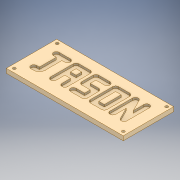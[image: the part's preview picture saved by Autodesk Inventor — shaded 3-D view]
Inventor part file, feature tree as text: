
AUTODESK INVENTOR PART (.ipt)
format: ipt  version: 2017 (Build 210142000, 142)  size: 520,192 bytes
history: native  units: mm
features: sketch x2, extrude x2
ambient origin geometry x8: Origin, YZ Plane, XZ Plane, XY Plane, X Axis, Y Axis, Z Axis, Center Point
bodies: Solid1 (feature_tree)
feature tree (4):
  sketch  "Sketch1"  dims[d2=26.0mm d3=6.5mm]
  extrude  "Extrusion1"  Depth=6.5mm
  extrude  "Extrusion2"  Depth=13.0mm
  sketch  "Sketch2"  dims[d4=13.0mm d11=13.0mm d12=6.5mm d13=13.0mm d16=39.0mm d17=39.0mm d18=6.5mm d19=52.0mm d20=6.5mm d22=13.0mm d23=19.5mm d24=13.0mm d29=13.0mm d30=13.0mm d31=13.0mm d32=13.0mm d35=26.0mm d36=52.0mm d37=13.0mm d38=6.5mm d39=6.5mm d46=19.5mm d49=6.5mm d50=6.5mm d51=90.0deg d52=6.5mm d53=26.0mm d54=6.5mm d55=26.0mm d56=19.5mm d57=39.0mm d58=13.0mm d59=13.0mm d60=19.5mm d61=13.0mm d62=19.5mm d63=26.0mm d64=13.0mm d65=39.0mm d66=13.0mm d67=52.0mm d68=6.5mm d69=39.0mm d70=13.0mm d71=39.0mm d72=13.0mm d73=13.0mm d74=6.5mm d75=90.0deg d76=26.0mm d77=13.0mm d78=6.5mm d79=6.5mm d84=13.0mm d86=26.0mm d87=13.0mm d89=52.0mm d90=13.0mm d93=6.5mm d94=6.5mm d95=6.5mm d96=6.5mm d97=6.5mm d98=13.0mm d99=6.35mm d100=6.35mm d101=6.35mm d102=6.35mm d103=10.0mm d104=0.0mm d105=5.0mm d106=0.0mm d107=269.0mm d108=116.0mm]
